# Revit family: Bath-Freestanding-KOHLER-Memoirs-K-8333_1
name_source: partatom
category: Plumbing Fixtures
revit_build: Autodesk Revit 2015 (Build: 20140606_1530(x64)
units: mm (PartAtom-declared; Revit-internal decimal feet)

## types (1)
- 0 - White
    ADA Compliant = No
    Assembly Code = D2010500
    CW Connection = No
    Cold Water Inlet = Cold Water Inlet
    Date Modified = 10/25/2018
    Default Elevation = 0"
    Description = 66 inch x 36 inch freestanding bath with center toe-tap drain
    Drain Included = Yes
    Finish = Kohler-Lithocast-0-White
    HW Connection = No
    Height = 23 3/4"
    Hot Water Inlet = Hot Water Inlet
    Length = 66 3/16"
    Manufacturer = KOHLER Co.
    MasterFormat 1995 = 15410
    MasterFormat 2004 = 22.41.19
    Material = Lithocast
    Model = K-8333-0
    Product Documentation Link = http://www.us.kohler.com
    Product Name = Memoirs
    Product Page URL = http://www.us.kohler.com
    URL = https://www.us.kohler.com
    Vent Connection = No
    Waste Connection = Yes
    Waste Water Outlet = Waste Water Outlet
    Width = 36 3/16"

## geometry (parser evidence)
native form markers: Sweep x6
no freeform markers — native parametric forms only
